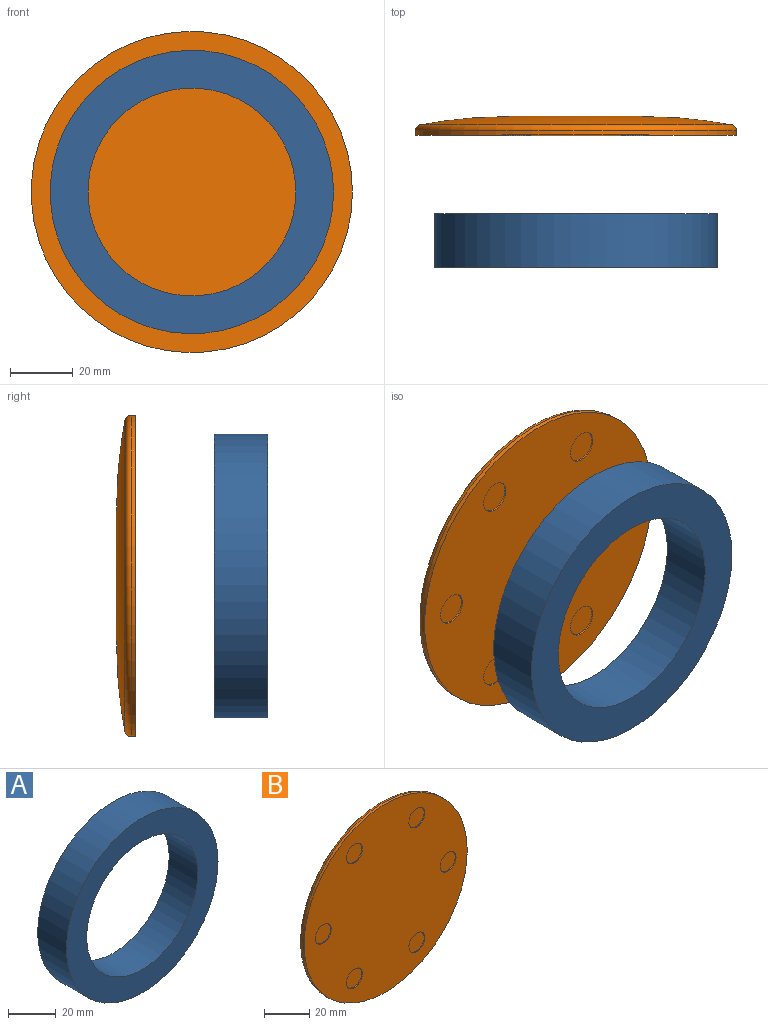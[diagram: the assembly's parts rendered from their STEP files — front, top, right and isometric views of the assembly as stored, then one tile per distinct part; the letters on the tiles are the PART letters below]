
ASSEMBLY  parts=2 mates=1
PART A: 16 faces, bbox 90x17x90 mm
  f0: cylinder r=33mm len=66mm, axis (0,1,0), area 3524.9mm2, adj f2,f3
  f1: cylinder r=45mm len=90mm, axis (0,1,0), area 4806.6mm2, adj f2,f3
  f2: plane 90x90mm, normal (0,-1,0), area 2940.5mm2, adj f0,f1
  f3: plane 90x90mm, normal (0,1,0), area 2469.3mm2, adj f0,f1,f4,f6,f8,f10,f12,f14
  f4: cylinder r=5mm len=10mm, axis (0,1,0), area 157.1mm2, adj f3,f5
  f5: plane 10x10mm, normal (0,1,0), area 78.5mm2, adj f4
  f6: cylinder r=5mm len=10mm, axis (0,1,0), area 157.1mm2, adj f3,f7
  f7: plane 10x10mm, normal (0,1,0), area 78.5mm2, adj f6
  f8: cylinder r=5mm len=10mm, axis (0,1,0), area 157.1mm2, adj f3,f9
  f9: plane 10x10mm, normal (0,1,0), area 78.5mm2, adj f8
  f10: cylinder r=5mm len=10mm, axis (0,1,0), area 157.1mm2, adj f3,f11
  f11: plane 10x10mm, normal (0,1,0), area 78.5mm2, adj f10
  f12: cylinder r=5mm len=10mm, axis (0,1,0), area 157.1mm2, adj f3,f13
  f13: plane 10x10mm, normal (0,1,0), area 78.5mm2, adj f12
  f14: cylinder r=5mm len=10mm, axis (0,1,0), area 157.1mm2, adj f3,f15
  f15: plane 10x10mm, normal (0,1,0), area 78.5mm2, adj f14
PART B: 17 faces, bbox 110.4x6.1x110.4 mm
  f0: cylinder r=51mm len=102mm, axis (0,-1,0), area 430.8mm2, adj f1,f4
  f1: torus R=49mm, axis (0,-1,0), area 879.5mm2, adj f0,f2
  f2: torus R=20mm, axis (0,-1,0), area 6441.9mm2, adj f1,f3
  f3: plane 40x40mm, normal (0,1,0), area 1256.6mm2, adj f2
  f4: plane 102x102mm, normal (0,-1,0), area 7700mm2, adj f0,f5,f7,f9,f11,f13,f15
  f5: cylinder r=5mm len=10mm, axis (0,-1,0), area 15.7mm2, adj f4,f6
  f6: plane 10x10mm, normal (0,-1,0), area 78.5mm2, adj f5
  f7: cylinder r=5mm len=10mm, axis (0,-1,0), area 15.7mm2, adj f4,f8
  f8: plane 10x10mm, normal (0,-1,0), area 78.5mm2, adj f7
  f9: cylinder r=5mm len=10mm, axis (0,-1,0), area 15.7mm2, adj f4,f10
  f10: plane 10x10mm, normal (0,-1,0), area 78.5mm2, adj f9
  f11: cylinder r=5mm len=10mm, axis (0,-1,0), area 15.7mm2, adj f4,f12
  f12: plane 10x10mm, normal (0,-1,0), area 78.5mm2, adj f11
  f13: cylinder r=5mm len=10mm, axis (0,-1,0), area 15.7mm2, adj f4,f14
  f14: plane 10x10mm, normal (0,-1,0), area 78.5mm2, adj f13
  f15: cylinder r=5mm len=10mm, axis (0,-1,0), area 15.7mm2, adj f4,f16
  f16: plane 10x10mm, normal (0,-1,0), area 78.5mm2, adj f15
PLACE A t=(-8.38,-24.7,12.2)mm
PLACE B t=(-8.38,0.3,12.2)mm
MATE planar A.f0 <-> B.f2  axis (0,1,0) through (-8.38,-24.7,12.2)mm
